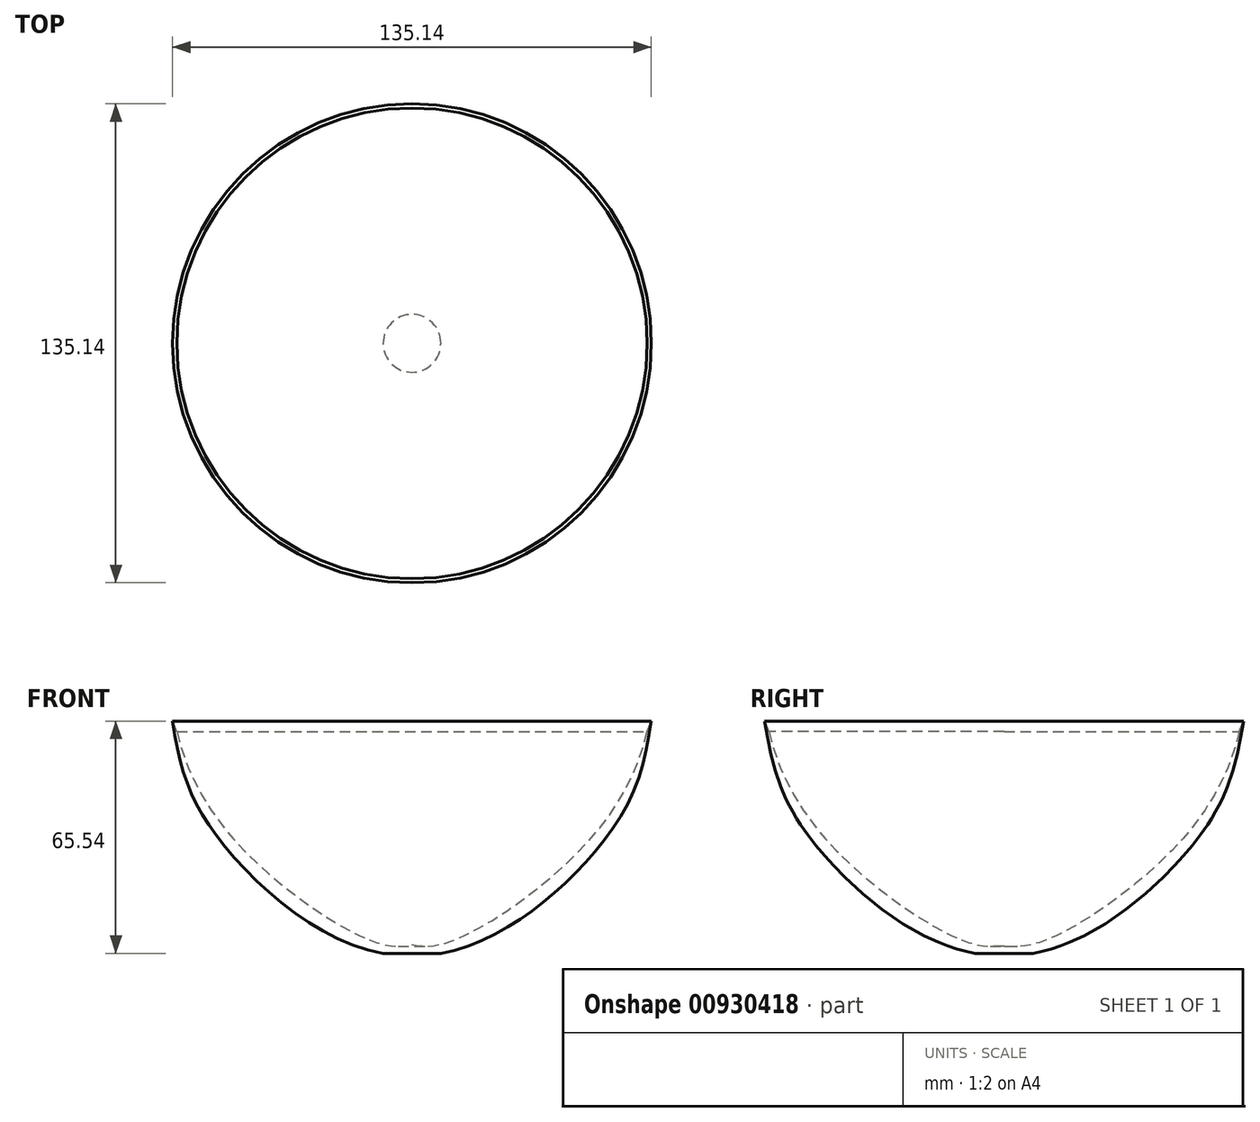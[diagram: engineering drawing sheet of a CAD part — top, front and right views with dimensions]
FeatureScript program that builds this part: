
annotation { "Feature Type Name" : "Feature", "Feature Type Description" : "" }
export const myFeature = defineFeature(function(context is Context, id is Id, definition is map)
    precondition{}
    {
        {
            var Q0;
            Q0=qCreatedBy(makeId("Front.planeOp"),FACE);
            var sketch = newSketch(context, id + "F0", { "sketchPlane" : qUnion([Q0])});
            skLineSegment(sketch, "E0", {"start": v(66.4, 59.39) * mm, "end": v(67.57, 62.34) * mm});
            skLineSegment(sketch, "E1", {"start": v(0, -3.2) * mm, "end": v(8.15, -3.2) * mm});
            skFitSpline(sketch, "E2", {"points": [v(67.57, 62.34) * mm, v(55, 29.72) * mm, v(8.15, -3.2) * mm], "startDerivative": vector(-14.27, -94.55) * mm, "endDerivative": vector(-99.62, -17.1) * mm});
            skLineSegment(sketch, "E3", {"start": v(0, -3.2) * mm, "end": v(0, -0.72) * mm});
            skFitSpline(sketch, "E4", {"points": [v(0, -0.72) * mm, v(10.44, 0) * mm, v(46.92, 25.35) * mm, v(66.4, 59.39) * mm], "startDerivative": vector(40.19, -9.73) * mm, "endDerivative": vector(23.12, 97.11) * mm});
            skSolve(sketch);
        }
        {
            var Q0;
            Q0 = qSketchRegion(id + "F0", true);
            var Q1;
            Q1=sQuery(id+"F0.wireOp",EDGE,"E3");
            revolve(context, id + "F1", {"surfaceOperationType" : NewSurfaceOperationType.NEW, "entities" : qUnion([Q0]), "axis" : qUnion([Q1]), "revolveType" : RevolveType.FULL});
        }
    });
